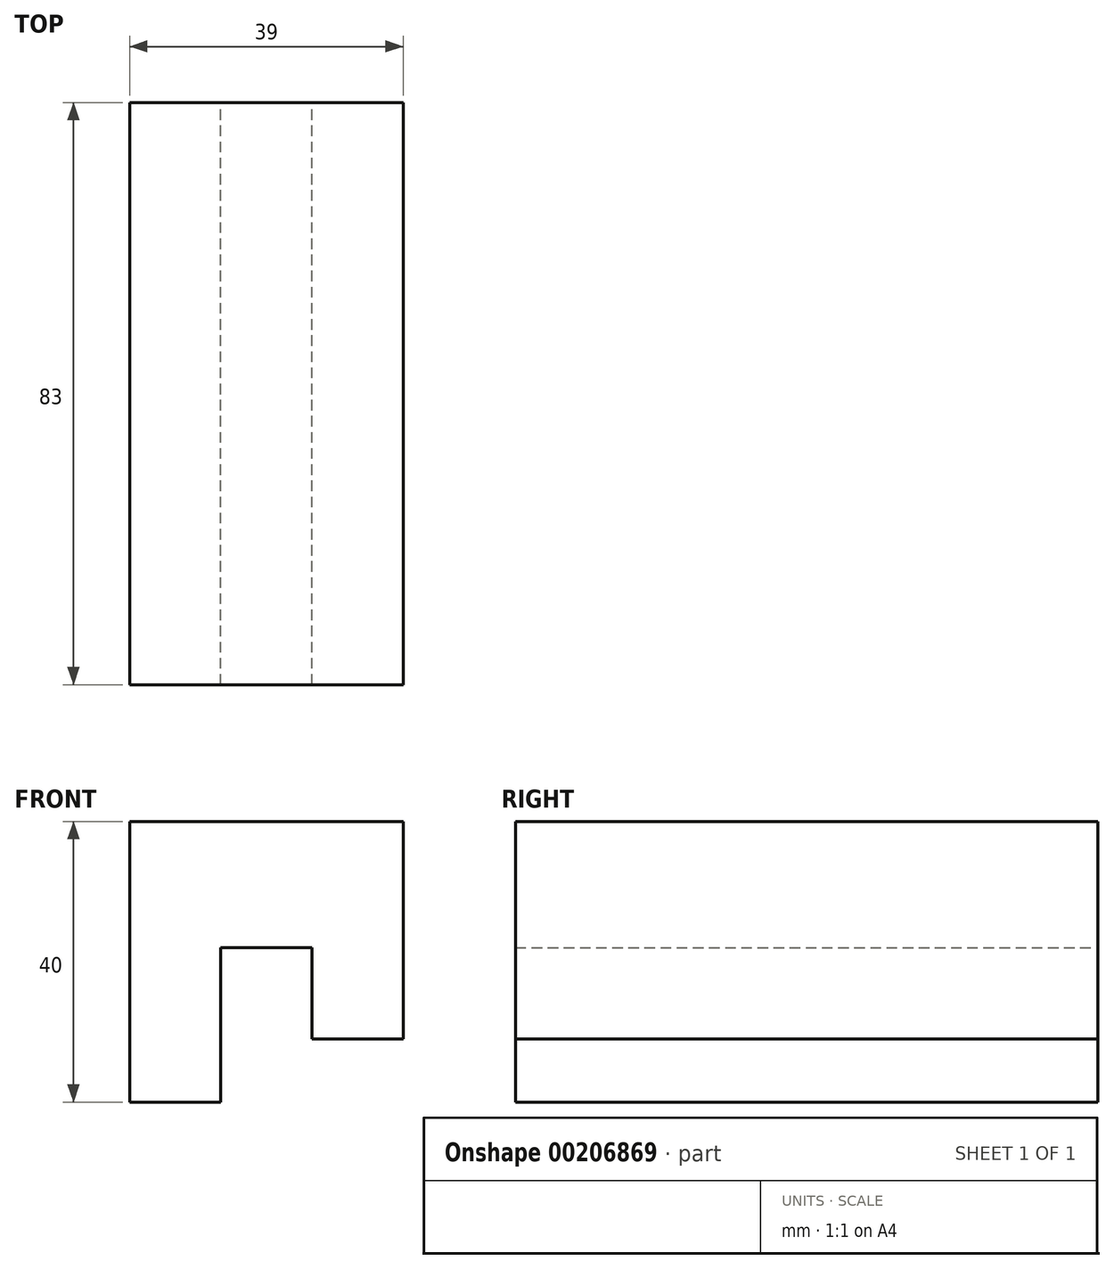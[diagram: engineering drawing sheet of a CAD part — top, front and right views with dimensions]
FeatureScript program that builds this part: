
annotation { "Feature Type Name" : "Feature", "Feature Type Description" : "" }
export const myFeature = defineFeature(function(context is Context, id is Id, definition is map)
    precondition{}
    {
        {
            var Q0;
            Q0=qCreatedBy(makeId("Front.planeOp"),FACE);
            var sketch = newSketch(context, id + "F0", { "sketchPlane" : qUnion([Q0])});
            skLineSegment(sketch, "E0", {"start": v(0, 0) * mm, "end": v(-13, 0) * mm});
            skLineSegment(sketch, "E1", {"start": v(-13, 0) * mm, "end": v(-13, 13) * mm});
            skLineSegment(sketch, "E2", {"start": v(-13, 13) * mm, "end": v(-26, 13) * mm});
            skLineSegment(sketch, "E3", {"start": v(-26, -9) * mm, "end": v(-39, -9) * mm});
            skLineSegment(sketch, "E4", {"start": v(-39, -9) * mm, "end": v(-39, 31) * mm});
            skLineSegment(sketch, "E5", {"start": v(-26, 13) * mm, "end": v(-26, -9) * mm});
            skLineSegment(sketch, "E6", {"start": v(-39, 31) * mm, "end": v(0, 31) * mm});
            skLineSegment(sketch, "E7", {"start": v(0, 31) * mm, "end": v(0, 0) * mm});
            skSolve(sketch);
        }
        {
            var Q0;
            Q0=makeQuery(id+"F0.imprint","IMPRINT",FACE,{"disambiguationData":[TD([[makeQuery(id+"F0.imprint","IMPRINT",EDGE,{"derivedFrom":sQuery(id+"F0.wireOp",EDGE,"E0")}),-1.0]])]});
            extrude(context, id + "F1", {"entities" : qUnion([Q0]), "depth" : 83 * mm});
        }
    });
